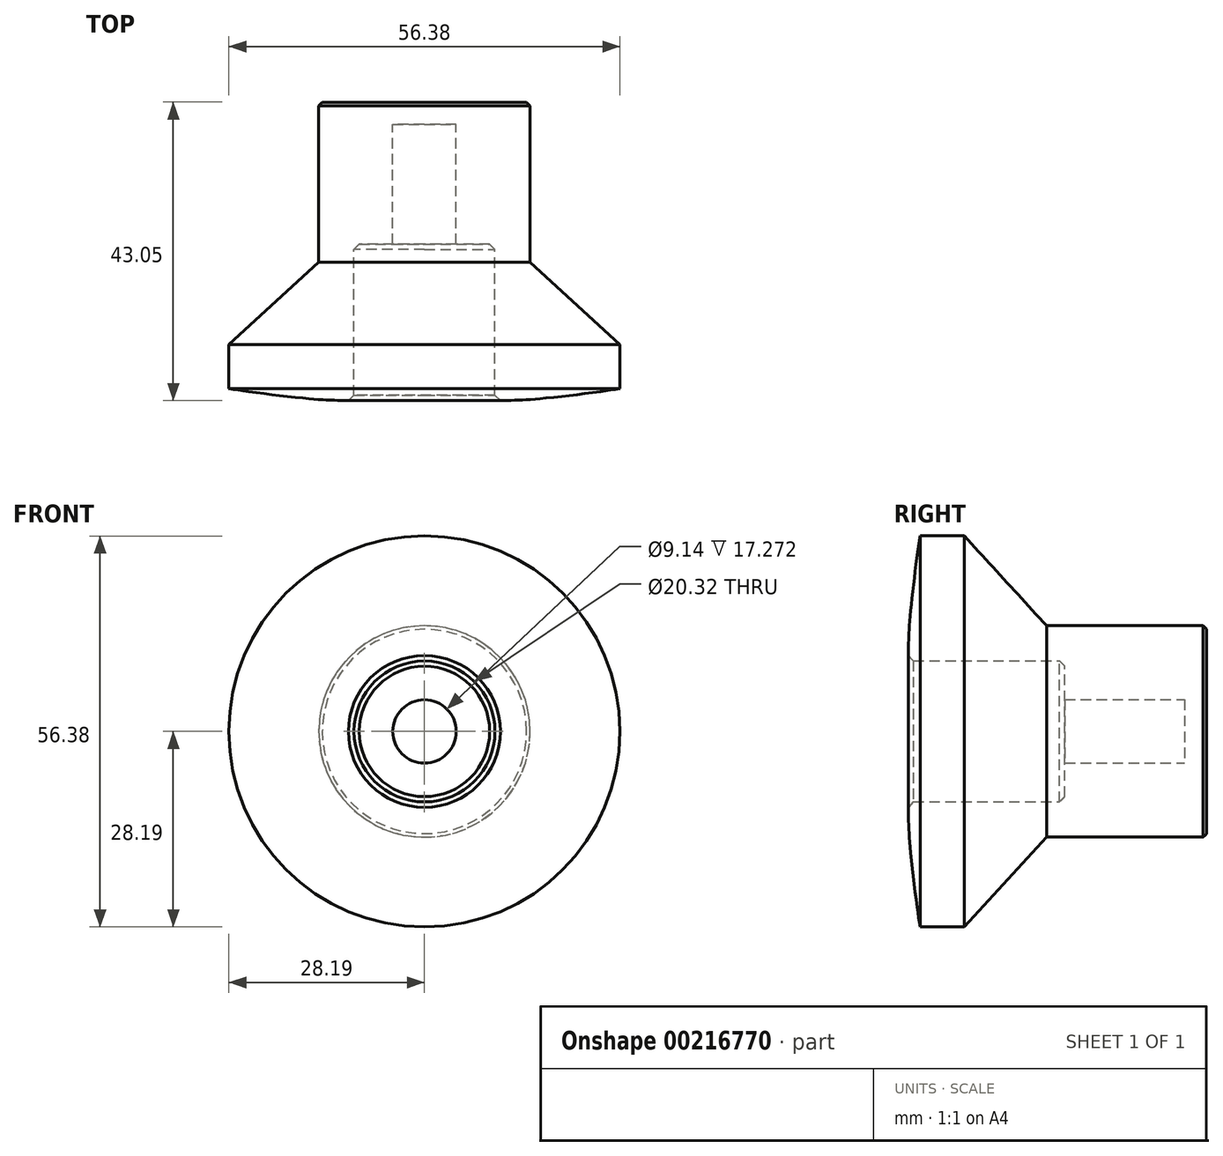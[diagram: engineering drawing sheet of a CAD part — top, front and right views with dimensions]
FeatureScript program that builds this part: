
annotation { "Feature Type Name" : "Feature", "Feature Type Description" : "" }
export const myFeature = defineFeature(function(context is Context, id is Id, definition is map)
    precondition{}
    {
        {
            var Q0;
            Q0=qCreatedBy(makeId("Top.planeOp"),FACE);
            var sketch = newSketch(context, id + "F0", { "sketchPlane" : qUnion([Q0])});
            skLineSegment(sketch, "E0", {"start": v(22.3, 37.24) * mm, "end": v(78.7, 37.24) * mm, "construction": true});
            skLineSegment(sketch, "E1", {"start": v(71.24, 6.38) * mm, "end": v(-26.07, 6.38) * mm, "construction": true});
            skLineSegment(sketch, "E2", {"start": v(-23.62, 39.32) * mm, "end": v(19.76, 39.32) * mm, "construction": true});
            skLineSegment(sketch, "E3", {"start": v(55.2, 22.91) * mm, "end": v(55.3, 22.91) * mm, "construction": true});
            skLineSegment(sketch, "E4", {"start": v(28.2, 0) * mm, "end": v(19.13, 0) * mm});
            skLineSegment(sketch, "E5", {"start": v(-23.62, 44.4) * mm, "end": v(55.2, 44.4) * mm, "construction": true});
            skLineSegment(sketch, "E6", {"start": v(-23.62, 64) * mm, "end": v(-23.62, -52.53) * mm, "construction": true});
            skPoint(sketch, "E7.orphan", {"position": v(0, 44.4) * mm});
            skPoint(sketch, "E8.orphan", {"position": v(0, 39.32) * mm});
            skArc(sketch, "E9", {"start": v(17.93, 40.19) * mm, "mid": v(9.17, 43.15) * mm, "end": v(0, 44.4) * mm, "construction": true});
            skLineSegment(sketch, "E10", {"start": v(0, 70.96) * mm, "end": v(0, 44.4) * mm, "construction": true});
            skLineSegment(sketch, "E11", {"start": v(0, 0) * mm, "end": v(0, 44.4) * mm});
            skPoint(sketch, "E12.visualSharp", {"position": v(19.76, 39.32) * mm});
            skLineSegment(sketch, "E13", {"start": v(-6.08, 43.64) * mm, "end": v(5.25, 43.64) * mm, "construction": true});
            skPoint(sketch, "E14", {"position": v(0, 43.64) * mm});
            skLineSegment(sketch, "E15", {"start": v(10.16, -1.78) * mm, "end": v(10.16, 20.83) * mm});
            skLineSegment(sketch, "E16", {"start": v(4.57, 20.83) * mm, "end": v(4.57, 38.1) * mm});
            skLineSegment(sketch, "E17", {"start": v(4.57, 38.1) * mm, "end": v(0, 38.1) * mm});
            skLineSegment(sketch, "E18.trimOffspring", {"start": v(0, 6.38) * mm, "end": v(0, -30.7) * mm, "construction": true});
            skPoint(sketch, "E19", {"position": v(9.17, 43.15) * mm});
            skLineSegment(sketch, "E20", {"start": v(28.2, 0) * mm, "end": v(28.2, 6.35) * mm});
            skLineSegment(sketch, "E21", {"start": v(28.2, 6.35) * mm, "end": v(15.24, 18.21) * mm});
            skLineSegment(sketch, "E22", {"start": v(15.24, 18.21) * mm, "end": v(15.24, 41.3) * mm});
            skPoint(sketch, "E23.1.internal.orphan", {"position": v(9.17, 42.64) * mm});
            skLineSegment(sketch, "E24", {"start": v(15.24, 41.3) * mm, "end": v(0, 41.3) * mm});
            skLineSegment(sketch, "E25.trimOffspring", {"start": v(0, 41.3) * mm, "end": v(0, 38.1) * mm, "construction": true});
            skLineSegment(sketch, "E26", {"start": v(10.16, 20.83) * mm, "end": v(4.57, 20.83) * mm});
            skFitSpline(sketch, "E27", {"points": [v(10.16, -1.78) * mm, v(15.52, -1.55) * mm, v(28.2, 0) * mm], "startDerivative": vector(20.31, 0.9) * mm, "endDerivative": vector(15.62, 2.71) * mm});
            skSolve(sketch);
        }
        {
            var Q0;
            Q0=qSketchRegion(id+"F0",true);
            var Q1;
            Q1=sQuery(id+"F0.wireOp",EDGE,"E10");
            revolve(context, id + "F1", {"entities" : qUnion([Q0]), "axis" : qUnion([Q1]), "revolveType" : RevolveType.FULL});
        }
        {
            var Q0;
            Q0=qCreatedBy(makeId("Front.planeOp"),FACE);
            var sketch = newSketch(context, id + "F4", { "sketchPlane" : qUnion([Q0])});
            skCircle(sketch, "E28", {"center": v(28.2, 0) * mm, "radius": 0.76 * mm});
            skLineSegment(sketch, "E29", {"start": v(35.15, 25.86) * mm, "end": v(35.15, -26.54) * mm, "construction": true});
            skSolve(sketch);
        }
        {
            var Q0;
            Q0=makeQuery(id+"F1.opRevolve","SWEPT_EDGE",EDGE,{"disambiguationData":[OSD([sQuery(id+"F0.wireOp",EDGE,"E15"),sQuery(id+"F0.wireOp",EDGE,"e01da25c-c68c-497c-a9d4-31c3cc3725c6")])]});
            chamfer(context, id + "F2", {"entities" : qUnion([Q0]), "width" : 0.76 * mm, "tangentPropagation" : true});
        }
        {
            var Q0;
            Q0=makeQuery(id+"F1.opRevolve","SWEPT_EDGE",EDGE,{"disambiguationData":[OSD([sQuery(id+"F0.wireOp",EDGE,"E22"),sQuery(id+"F0.wireOp",EDGE,"E24")])]});
            chamfer(context, id + "F3", {"entities" : qUnion([Q0]), "width" : 0.5 * mm, "tangentPropagation" : true});
        }
    });
